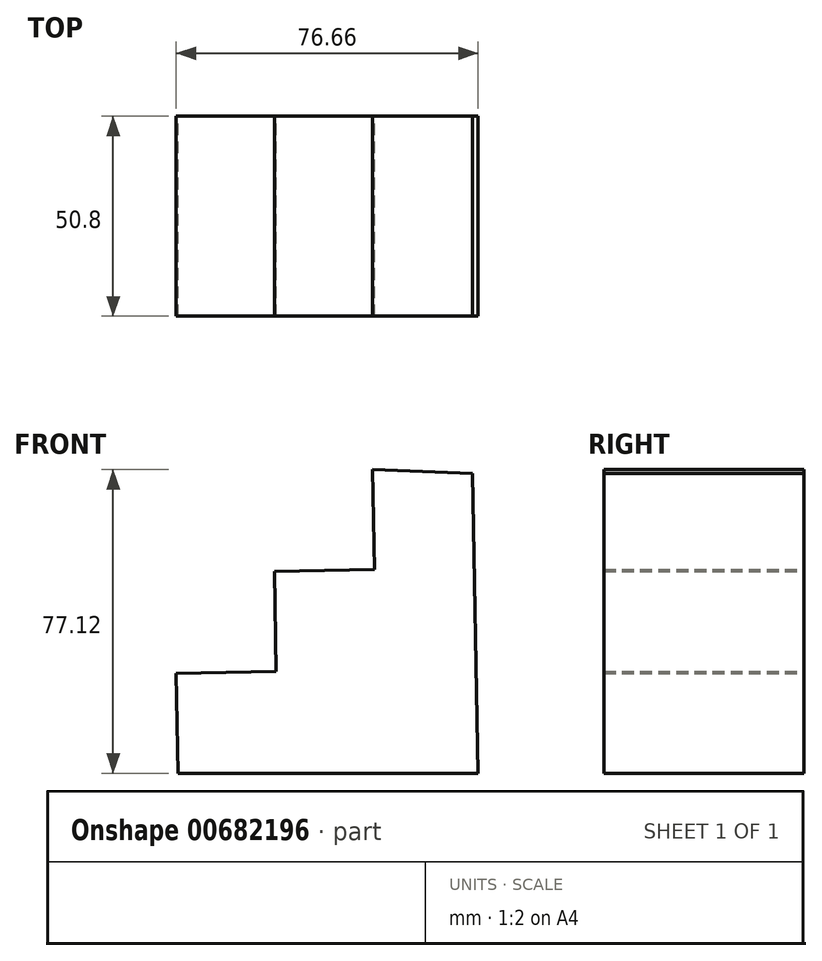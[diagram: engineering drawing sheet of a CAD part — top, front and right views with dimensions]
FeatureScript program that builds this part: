
annotation { "Feature Type Name" : "Feature", "Feature Type Description" : "" }
export const myFeature = defineFeature(function(context is Context, id is Id, definition is map)
    precondition{}
    {
        {
            var Q0;
            Q0=qCreatedBy(makeId("Front.planeOp"),FACE);
            var sketch = newSketch(context, id + "F0", { "sketchPlane" : qUnion([Q0])});
            skLineSegment(sketch, "E0", {"start": v(58.1, 32.96) * mm, "end": v(59.5, -43.23) * mm});
            skLineSegment(sketch, "E1", {"start": v(59.5, -43.23) * mm, "end": v(-16.7, -43.23) * mm});
            skLineSegment(sketch, "E2", {"start": v(-16.7, -43.23) * mm, "end": v(-17.16, -17.83) * mm});
            skLineSegment(sketch, "E3", {"start": v(-17.16, -17.83) * mm, "end": v(8.23, -17.37) * mm});
            skLineSegment(sketch, "E4", {"start": v(8.23, -17.37) * mm, "end": v(7.77, 8.03) * mm});
            skLineSegment(sketch, "E5", {"start": v(7.77, 8.03) * mm, "end": v(33.16, 8.5) * mm});
            skLineSegment(sketch, "E6", {"start": v(33.16, 8.5) * mm, "end": v(32.7, 33.89) * mm});
            skLineSegment(sketch, "E7", {"start": v(32.7, 33.89) * mm, "end": v(58.1, 32.96) * mm});
            skSolve(sketch);
        }
        {
            var Q0;
            Q0 = qSketchRegion(id + "F0", true);
            extrude(context, id + "F1", {"entities" : qUnion([Q0]), "depth" : 50.8 * mm, "offsetDistance" : 25.4 * mm});
        }
    });
